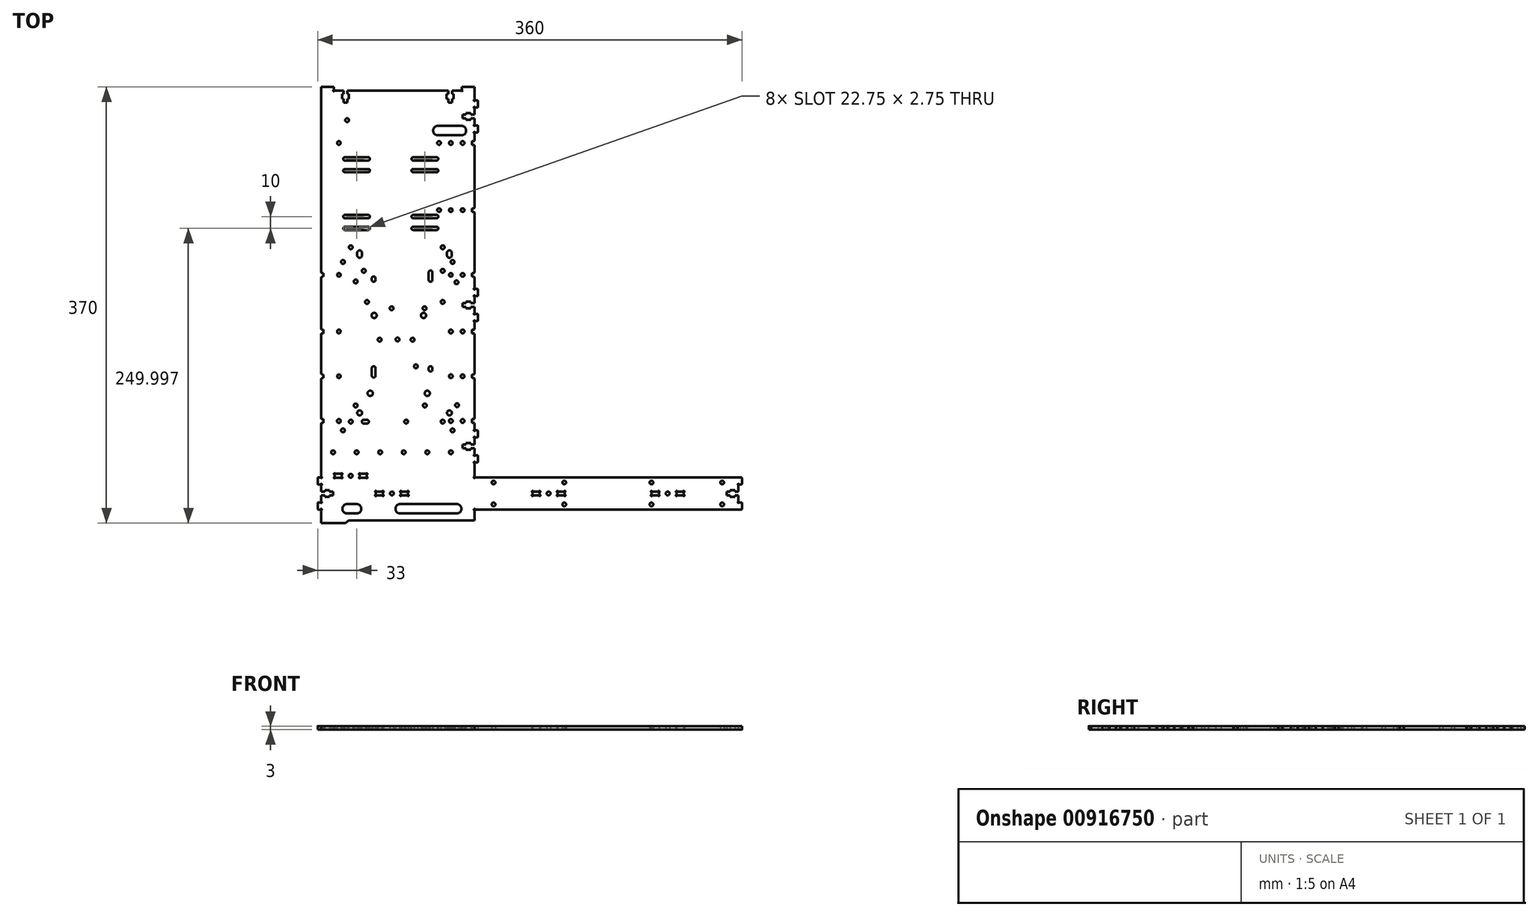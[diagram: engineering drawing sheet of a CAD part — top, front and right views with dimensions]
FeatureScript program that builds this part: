
annotation { "Feature Type Name" : "Feature", "Feature Type Description" : "" }
export const myFeature = defineFeature(function(context is Context, id is Id, definition is map)
    precondition{}
    {
        {
            var Q0;
            Q0=qCreatedBy(makeId("Top.planeOp"),FACE);
            var sketch = newSketch(context, id + "F0", { "sketchPlane" : qUnion([Q0])});
            skCircle(sketch, "E0", {"center": v(103.25, -146.86) * mm, "radius": 1.55 * mm});
            skCircle(sketch, "E1", {"center": v(-30.75, -146.86) * mm, "radius": 1.55 * mm});
            skCircle(sketch, "E2", {"center": v(163.25, -165.45) * mm, "radius": 1.55 * mm});
            skCircle(sketch, "E3", {"center": v(-30.75, -165.45) * mm, "radius": 1.55 * mm});
            skArc(sketch, "E4", {"start": v(104.17, -157.8) * mm, "mid": v(103.92, -157.87) * mm, "end": v(103.73, -158.05) * mm});
            skArc(sketch, "E5", {"start": v(103.05, -157.37) * mm, "mid": v(102.95, -158.16) * mm, "end": v(103.73, -158.05) * mm});
            skArc(sketch, "E6", {"start": v(103.05, -157.37) * mm, "mid": v(103.23, -157.19) * mm, "end": v(103.3, -156.94) * mm});
            skLineSegment(sketch, "E7", {"start": v(103.3, -155.37) * mm, "end": v(103.3, -156.94) * mm});
            skArc(sketch, "E8", {"start": v(103.3, -155.37) * mm, "mid": v(103.23, -155.12) * mm, "end": v(103.05, -154.94) * mm});
            skArc(sketch, "E9", {"start": v(103.73, -154.25) * mm, "mid": v(102.95, -154.15) * mm, "end": v(103.05, -154.94) * mm});
            skArc(sketch, "E10", {"start": v(103.73, -154.25) * mm, "mid": v(103.92, -154.44) * mm, "end": v(104.17, -154.5) * mm});
            skLineSegment(sketch, "E11", {"start": v(108.63, -154.5) * mm, "end": v(104.17, -154.5) * mm});
            skArc(sketch, "E12", {"start": v(108.63, -154.5) * mm, "mid": v(108.88, -154.44) * mm, "end": v(109.07, -154.25) * mm});
            skArc(sketch, "E13", {"start": v(109.75, -154.94) * mm, "mid": v(109.85, -154.15) * mm, "end": v(109.07, -154.25) * mm});
            skArc(sketch, "E14", {"start": v(109.75, -154.94) * mm, "mid": v(109.57, -155.12) * mm, "end": v(109.5, -155.37) * mm});
            skLineSegment(sketch, "E15", {"start": v(109.5, -156.94) * mm, "end": v(109.5, -155.37) * mm});
            skArc(sketch, "E16", {"start": v(109.5, -156.94) * mm, "mid": v(109.57, -157.19) * mm, "end": v(109.75, -157.37) * mm});
            skArc(sketch, "E17", {"start": v(109.07, -158.05) * mm, "mid": v(109.85, -158.16) * mm, "end": v(109.75, -157.37) * mm});
            skArc(sketch, "E18", {"start": v(109.07, -158.05) * mm, "mid": v(108.88, -157.87) * mm, "end": v(108.63, -157.8) * mm});
            skLineSegment(sketch, "E19", {"start": v(104.17, -157.8) * mm, "end": v(108.63, -157.8) * mm});
            skArc(sketch, "E20", {"start": v(125.37, -157.8) * mm, "mid": v(125.12, -157.87) * mm, "end": v(124.93, -158.05) * mm});
            skArc(sketch, "E21", {"start": v(124.25, -157.37) * mm, "mid": v(124.15, -158.16) * mm, "end": v(124.93, -158.05) * mm});
            skArc(sketch, "E22", {"start": v(124.25, -157.37) * mm, "mid": v(124.43, -157.19) * mm, "end": v(124.5, -156.94) * mm});
            skLineSegment(sketch, "E23", {"start": v(124.5, -155.37) * mm, "end": v(124.5, -156.94) * mm});
            skArc(sketch, "E24", {"start": v(124.5, -155.37) * mm, "mid": v(124.43, -155.12) * mm, "end": v(124.25, -154.94) * mm});
            skArc(sketch, "E25", {"start": v(124.93, -154.25) * mm, "mid": v(124.15, -154.15) * mm, "end": v(124.25, -154.94) * mm});
            skArc(sketch, "E26", {"start": v(124.93, -154.25) * mm, "mid": v(125.12, -154.44) * mm, "end": v(125.37, -154.5) * mm});
            skLineSegment(sketch, "E27", {"start": v(129.83, -154.5) * mm, "end": v(125.37, -154.5) * mm});
            skArc(sketch, "E28", {"start": v(129.83, -154.5) * mm, "mid": v(130.08, -154.44) * mm, "end": v(130.27, -154.25) * mm});
            skArc(sketch, "E29", {"start": v(130.95, -154.94) * mm, "mid": v(131.05, -154.15) * mm, "end": v(130.27, -154.25) * mm});
            skArc(sketch, "E30", {"start": v(130.95, -154.94) * mm, "mid": v(130.77, -155.12) * mm, "end": v(130.7, -155.37) * mm});
            skLineSegment(sketch, "E31", {"start": v(130.7, -156.94) * mm, "end": v(130.7, -155.37) * mm});
            skArc(sketch, "E32", {"start": v(130.7, -156.94) * mm, "mid": v(130.77, -157.19) * mm, "end": v(130.95, -157.37) * mm});
            skArc(sketch, "E33", {"start": v(130.27, -158.05) * mm, "mid": v(131.05, -158.16) * mm, "end": v(130.95, -157.37) * mm});
            skArc(sketch, "E34", {"start": v(130.27, -158.05) * mm, "mid": v(130.08, -157.87) * mm, "end": v(129.83, -157.8) * mm});
            skLineSegment(sketch, "E35", {"start": v(125.37, -157.8) * mm, "end": v(129.83, -157.8) * mm});
            skCircle(sketch, "E36", {"center": v(-67, 29.35) * mm, "radius": 1.55 * mm});
            skCircle(sketch, "E37", {"center": v(-77, 84.35) * mm, "radius": 1.55 * mm});
            skCircle(sketch, "E38", {"center": v(-73.88, 52.83) * mm, "radius": 1.6 * mm});
            skCircle(sketch, "E39", {"center": v(-151.88, -95.17) * mm, "radius": 1.6 * mm});
            skCircle(sketch, "E40", {"center": v(-90.17, -5.05) * mm, "radius": 2.23 * mm});
            skCircle(sketch, "E41", {"center": v(-87, -71.15) * mm, "radius": 2.23 * mm});
            skCircle(sketch, "E42", {"center": v(-87, -121.15) * mm, "radius": 1.6 * mm});
            skCircle(sketch, "E43", {"center": v(-127, -121.15) * mm, "radius": 1.6 * mm});
            skCircle(sketch, "E44", {"center": v(-167, -121.15) * mm, "radius": 1.6 * mm});
            skCircle(sketch, "E45", {"center": v(-162, -56.65) * mm, "radius": 1.55 * mm});
            skCircle(sketch, "E46", {"center": v(-162, 29.35) * mm, "radius": 1.55 * mm});
            skCircle(sketch, "E47", {"center": v(-140.88, 32.83) * mm, "radius": 1.6 * mm});
            skCircle(sketch, "E48", {"center": v(-73.88, 32.83) * mm, "radius": 1.6 * mm});
            skCircle(sketch, "E49", {"center": v(-65.5, 40.35) * mm, "radius": 1.6 * mm});
            skCircle(sketch, "E50", {"center": v(-65.5, -102.65) * mm, "radius": 1.6 * mm});
            skCircle(sketch, "E51", {"center": v(-112.23, -25.44) * mm, "radius": 1.6 * mm});
            skCircle(sketch, "E52", {"center": v(-61.73, -81.24) * mm, "radius": 1.6 * mm});
            skCircle(sketch, "E53", {"center": v(-147.73, 23.76) * mm, "radius": 1.6 * mm});
            skCircle(sketch, "E54", {"center": v(-62.23, 23.06) * mm, "radius": 1.6 * mm});
            skCircle(sketch, "E55", {"center": v(-73.88, 6.43) * mm, "radius": 1.6 * mm});
            skLineSegment(sketch, "E56", {"start": v(-134.07, 26.46) * mm, "end": v(-134.07, 25.19) * mm});
            skArc(sketch, "E57", {"start": v(-130.87, 26.46) * mm, "mid": v(-132.47, 28.06) * mm, "end": v(-134.07, 26.46) * mm});
            skLineSegment(sketch, "E58", {"start": v(-130.87, 25.19) * mm, "end": v(-130.87, 26.46) * mm});
            skArc(sketch, "E59", {"start": v(-134.07, 25.19) * mm, "mid": v(-132.47, 23.59) * mm, "end": v(-130.87, 25.19) * mm});
            skCircle(sketch, "E60", {"center": v(-127.39, -25.61) * mm, "radius": 1.6 * mm});
            skCircle(sketch, "E61", {"center": v(-99.45, -25.61) * mm, "radius": 1.6 * mm});
            skCircle(sketch, "E62", {"center": v(-57, 141.35) * mm, "radius": 1.55 * mm});
            skCircle(sketch, "E63", {"center": v(-67, -18.65) * mm, "radius": 1.6 * mm});
            skCircle(sketch, "E64", {"center": v(-67, -94.65) * mm, "radius": 1.6 * mm});
            skCircle(sketch, "E65", {"center": v(-57, -56.65) * mm, "radius": 1.55 * mm});
            skCircle(sketch, "E66", {"center": v(-57, -18.65) * mm, "radius": 1.55 * mm});
            skCircle(sketch, "E67", {"center": v(-152, -141.15) * mm, "radius": 1.6 * mm});
            skArc(sketch, "E68", {"start": v(-129.83, -157.8) * mm, "mid": v(-130.08, -157.87) * mm, "end": v(-130.27, -158.05) * mm});
            skArc(sketch, "E69", {"start": v(-130.95, -157.37) * mm, "mid": v(-131.05, -158.16) * mm, "end": v(-130.27, -158.05) * mm});
            skArc(sketch, "E70", {"start": v(-130.95, -157.37) * mm, "mid": v(-130.77, -157.19) * mm, "end": v(-130.7, -156.94) * mm});
            skLineSegment(sketch, "E71", {"start": v(-130.7, -155.37) * mm, "end": v(-130.7, -156.94) * mm});
            skArc(sketch, "E72", {"start": v(-130.7, -155.37) * mm, "mid": v(-130.77, -155.12) * mm, "end": v(-130.95, -154.94) * mm});
            skArc(sketch, "E73", {"start": v(-130.27, -154.25) * mm, "mid": v(-131.05, -154.15) * mm, "end": v(-130.95, -154.94) * mm});
            skArc(sketch, "E74", {"start": v(-130.27, -154.25) * mm, "mid": v(-130.08, -154.44) * mm, "end": v(-129.83, -154.5) * mm});
            skLineSegment(sketch, "E75", {"start": v(-125.37, -154.5) * mm, "end": v(-129.83, -154.5) * mm});
            skArc(sketch, "E76", {"start": v(-125.37, -154.5) * mm, "mid": v(-125.12, -154.44) * mm, "end": v(-124.93, -154.25) * mm});
            skArc(sketch, "E77", {"start": v(-124.25, -154.94) * mm, "mid": v(-124.15, -154.15) * mm, "end": v(-124.93, -154.25) * mm});
            skArc(sketch, "E78", {"start": v(-124.25, -154.94) * mm, "mid": v(-124.43, -155.12) * mm, "end": v(-124.5, -155.37) * mm});
            skLineSegment(sketch, "E79", {"start": v(-124.5, -156.94) * mm, "end": v(-124.5, -155.37) * mm});
            skArc(sketch, "E80", {"start": v(-124.5, -156.94) * mm, "mid": v(-124.43, -157.19) * mm, "end": v(-124.25, -157.37) * mm});
            skArc(sketch, "E81", {"start": v(-124.93, -158.05) * mm, "mid": v(-124.15, -158.16) * mm, "end": v(-124.25, -157.37) * mm});
            skArc(sketch, "E82", {"start": v(-124.93, -158.05) * mm, "mid": v(-125.12, -157.87) * mm, "end": v(-125.37, -157.8) * mm});
            skLineSegment(sketch, "E83", {"start": v(-129.83, -157.8) * mm, "end": v(-125.37, -157.8) * mm});
            skArc(sketch, "E84", {"start": v(-108.63, -157.8) * mm, "mid": v(-108.88, -157.87) * mm, "end": v(-109.07, -158.05) * mm});
            skArc(sketch, "E85", {"start": v(-109.75, -157.37) * mm, "mid": v(-109.85, -158.16) * mm, "end": v(-109.07, -158.05) * mm});
            skArc(sketch, "E86", {"start": v(-109.75, -157.37) * mm, "mid": v(-109.57, -157.19) * mm, "end": v(-109.5, -156.94) * mm});
            skLineSegment(sketch, "E87", {"start": v(-109.5, -155.37) * mm, "end": v(-109.5, -156.94) * mm});
            skArc(sketch, "E88", {"start": v(-109.5, -155.37) * mm, "mid": v(-109.57, -155.12) * mm, "end": v(-109.75, -154.94) * mm});
            skArc(sketch, "E89", {"start": v(-109.07, -154.25) * mm, "mid": v(-109.85, -154.15) * mm, "end": v(-109.75, -154.94) * mm});
            skArc(sketch, "E90", {"start": v(-109.07, -154.25) * mm, "mid": v(-108.88, -154.44) * mm, "end": v(-108.63, -154.5) * mm});
            skLineSegment(sketch, "E91", {"start": v(-104.17, -154.5) * mm, "end": v(-108.63, -154.5) * mm});
            skArc(sketch, "E92", {"start": v(-104.17, -154.5) * mm, "mid": v(-103.92, -154.44) * mm, "end": v(-103.73, -154.25) * mm});
            skArc(sketch, "E93", {"start": v(-103.05, -154.94) * mm, "mid": v(-102.95, -154.15) * mm, "end": v(-103.73, -154.25) * mm});
            skArc(sketch, "E94", {"start": v(-103.05, -154.94) * mm, "mid": v(-103.23, -155.12) * mm, "end": v(-103.3, -155.37) * mm});
            skLineSegment(sketch, "E95", {"start": v(-103.3, -156.94) * mm, "end": v(-103.3, -155.37) * mm});
            skArc(sketch, "E96", {"start": v(-103.3, -156.94) * mm, "mid": v(-103.23, -157.19) * mm, "end": v(-103.05, -157.37) * mm});
            skArc(sketch, "E97", {"start": v(-103.73, -158.05) * mm, "mid": v(-102.95, -158.16) * mm, "end": v(-103.05, -157.37) * mm});
            skArc(sketch, "E98", {"start": v(-103.73, -158.05) * mm, "mid": v(-103.92, -157.87) * mm, "end": v(-104.17, -157.8) * mm});
            skLineSegment(sketch, "E99", {"start": v(-108.63, -157.8) * mm, "end": v(-104.17, -157.8) * mm});
            skLineSegment(sketch, "E100", {"start": v(-155, -173.15) * mm, "end": v(-147, -173.15) * mm});
            skArc(sketch, "E101", {"start": v(-155, -165.15) * mm, "mid": v(-159, -169.15) * mm, "end": v(-155, -173.15) * mm});
            skLineSegment(sketch, "E102", {"start": v(-147, -165.15) * mm, "end": v(-155, -165.15) * mm});
            skArc(sketch, "E103", {"start": v(-147, -173.15) * mm, "mid": v(-143, -169.15) * mm, "end": v(-147, -165.15) * mm});
            skCircle(sketch, "E104", {"center": v(-155, 160.75) * mm, "radius": 1.6 * mm});
            skCircle(sketch, "E105", {"center": v(16, -156.15) * mm, "radius": 1.6 * mm});
            skArc(sketch, "E106", {"start": v(-47, -170.62) * mm, "mid": v(-47.07, -170.37) * mm, "end": v(-47.25, -170.19) * mm});
            skArc(sketch, "E107", {"start": v(-46.57, -169.5) * mm, "mid": v(-47.35, -169.4) * mm, "end": v(-47.25, -170.19) * mm});
            skArc(sketch, "E108", {"start": v(-46.57, -169.5) * mm, "mid": v(-46.38, -169.69) * mm, "end": v(-46.13, -169.75) * mm});
            skLineSegment(sketch, "E109", {"start": v(-46.13, -169.75) * mm, "end": v(179.5, -169.75) * mm});
            skArc(sketch, "E110", {"start": v(179.5, -169.75) * mm, "mid": v(179.85, -169.6) * mm, "end": v(180, -169.25) * mm});
            skLineSegment(sketch, "E111", {"start": v(180, -169.25) * mm, "end": v(180, -164.25) * mm});
            skArc(sketch, "E112", {"start": v(180, -164.25) * mm, "mid": v(179.85, -163.9) * mm, "end": v(179.5, -163.75) * mm});
            skLineSegment(sketch, "E113", {"start": v(179.5, -163.75) * mm, "end": v(177.87, -163.75) * mm});
            skArc(sketch, "E114", {"start": v(177.87, -163.75) * mm, "mid": v(177.62, -163.82) * mm, "end": v(177.43, -164) * mm});
            skArc(sketch, "E115", {"start": v(176.75, -163.32) * mm, "mid": v(176.65, -164.1) * mm, "end": v(177.43, -164) * mm});
            skArc(sketch, "E116", {"start": v(176.75, -163.32) * mm, "mid": v(176.93, -163.14) * mm, "end": v(177, -162.89) * mm});
            skLineSegment(sketch, "E117", {"start": v(177, -162.89) * mm, "end": v(177, -157.75) * mm});
            skLineSegment(sketch, "E118", {"start": v(177, -157.75) * mm, "end": v(174, -157.75) * mm});
            skLineSegment(sketch, "E119", {"start": v(174, -157.75) * mm, "end": v(174, -159.03) * mm});
            skLineSegment(sketch, "E120", {"start": v(174, -159.03) * mm, "end": v(170, -159.03) * mm});
            skLineSegment(sketch, "E121", {"start": v(170, -159.03) * mm, "end": v(170, -157.75) * mm});
            skLineSegment(sketch, "E122", {"start": v(170, -157.75) * mm, "end": v(167, -157.75) * mm});
            skLineSegment(sketch, "E123", {"start": v(167, -157.75) * mm, "end": v(167, -154.55) * mm});
            skLineSegment(sketch, "E124", {"start": v(167, -154.55) * mm, "end": v(170, -154.55) * mm});
            skLineSegment(sketch, "E125", {"start": v(170, -154.55) * mm, "end": v(170, -153.28) * mm});
            skLineSegment(sketch, "E126", {"start": v(170, -153.28) * mm, "end": v(174, -153.28) * mm});
            skLineSegment(sketch, "E127", {"start": v(174, -153.28) * mm, "end": v(174, -154.55) * mm});
            skLineSegment(sketch, "E128", {"start": v(174, -154.55) * mm, "end": v(177, -154.55) * mm});
            skLineSegment(sketch, "E129", {"start": v(177, -154.55) * mm, "end": v(177, -149.42) * mm});
            skArc(sketch, "E130", {"start": v(177, -149.42) * mm, "mid": v(176.93, -149.17) * mm, "end": v(176.75, -148.99) * mm});
            skArc(sketch, "E131", {"start": v(177.43, -148.3) * mm, "mid": v(176.65, -148.2) * mm, "end": v(176.75, -148.99) * mm});
            skArc(sketch, "E132", {"start": v(177.43, -148.3) * mm, "mid": v(177.62, -148.49) * mm, "end": v(177.87, -148.55) * mm});
            skLineSegment(sketch, "E133", {"start": v(177.87, -148.55) * mm, "end": v(179.5, -148.55) * mm});
            skArc(sketch, "E134", {"start": v(179.5, -148.55) * mm, "mid": v(179.85, -148.4) * mm, "end": v(180, -148.05) * mm});
            skLineSegment(sketch, "E135", {"start": v(180, -148.05) * mm, "end": v(180, -143.05) * mm});
            skArc(sketch, "E136", {"start": v(180, -143.05) * mm, "mid": v(179.85, -142.7) * mm, "end": v(179.5, -142.55) * mm});
            skLineSegment(sketch, "E137", {"start": v(179.5, -142.55) * mm, "end": v(-46.13, -142.55) * mm});
            skArc(sketch, "E138", {"start": v(-46.13, -142.55) * mm, "mid": v(-46.38, -142.62) * mm, "end": v(-46.57, -142.8) * mm});
            skArc(sketch, "E139", {"start": v(-47.25, -142.12) * mm, "mid": v(-47.35, -142.9) * mm, "end": v(-46.57, -142.8) * mm});
            skArc(sketch, "E140", {"start": v(-47.25, -142.12) * mm, "mid": v(-47.07, -141.94) * mm, "end": v(-47, -141.69) * mm});
            skLineSegment(sketch, "E141", {"start": v(-47, -141.69) * mm, "end": v(-47, -130.62) * mm});
            skArc(sketch, "E142", {"start": v(-47, -130.62) * mm, "mid": v(-47.07, -130.37) * mm, "end": v(-47.25, -130.19) * mm});
            skArc(sketch, "E143", {"start": v(-46.57, -129.5) * mm, "mid": v(-47.35, -129.4) * mm, "end": v(-47.25, -130.19) * mm});
            skArc(sketch, "E144", {"start": v(-46.57, -129.5) * mm, "mid": v(-46.38, -129.69) * mm, "end": v(-46.13, -129.75) * mm});
            skLineSegment(sketch, "E145", {"start": v(-46.13, -129.75) * mm, "end": v(-44.5, -129.75) * mm});
            skArc(sketch, "E146", {"start": v(-44.5, -129.75) * mm, "mid": v(-44.15, -129.6) * mm, "end": v(-44, -129.25) * mm});
            skLineSegment(sketch, "E147", {"start": v(-44, -129.25) * mm, "end": v(-44, -124.25) * mm});
            skArc(sketch, "E148", {"start": v(-44, -124.25) * mm, "mid": v(-44.15, -123.9) * mm, "end": v(-44.5, -123.75) * mm});
            skLineSegment(sketch, "E149", {"start": v(-44.5, -123.75) * mm, "end": v(-46.13, -123.75) * mm});
            skArc(sketch, "E150", {"start": v(-46.13, -123.75) * mm, "mid": v(-46.38, -123.82) * mm, "end": v(-46.57, -124) * mm});
            skArc(sketch, "E151", {"start": v(-47.25, -123.32) * mm, "mid": v(-47.35, -124.1) * mm, "end": v(-46.57, -124) * mm});
            skArc(sketch, "E152", {"start": v(-47.25, -123.32) * mm, "mid": v(-47.07, -123.14) * mm, "end": v(-47, -122.89) * mm});
            skLineSegment(sketch, "E153", {"start": v(-47, -122.89) * mm, "end": v(-47, -117.75) * mm});
            skLineSegment(sketch, "E154", {"start": v(-47, -117.75) * mm, "end": v(-50, -117.75) * mm});
            skLineSegment(sketch, "E155", {"start": v(-50, -117.75) * mm, "end": v(-50, -119.03) * mm});
            skLineSegment(sketch, "E156", {"start": v(-50, -119.03) * mm, "end": v(-54, -119.03) * mm});
            skLineSegment(sketch, "E157", {"start": v(-54, -119.03) * mm, "end": v(-54, -117.75) * mm});
            skLineSegment(sketch, "E158", {"start": v(-54, -117.75) * mm, "end": v(-57, -117.75) * mm});
            skLineSegment(sketch, "E159", {"start": v(-57, -117.75) * mm, "end": v(-57, -114.55) * mm});
            skLineSegment(sketch, "E160", {"start": v(-57, -114.55) * mm, "end": v(-54, -114.55) * mm});
            skLineSegment(sketch, "E161", {"start": v(-54, -114.55) * mm, "end": v(-54, -113.28) * mm});
            skLineSegment(sketch, "E162", {"start": v(-54, -113.28) * mm, "end": v(-50, -113.28) * mm});
            skLineSegment(sketch, "E163", {"start": v(-50, -113.28) * mm, "end": v(-50, -114.55) * mm});
            skLineSegment(sketch, "E164", {"start": v(-50, -114.55) * mm, "end": v(-47, -114.55) * mm});
            skLineSegment(sketch, "E165", {"start": v(-47, -114.55) * mm, "end": v(-47, -109.42) * mm});
            skArc(sketch, "E166", {"start": v(-47, -109.42) * mm, "mid": v(-47.07, -109.17) * mm, "end": v(-47.25, -108.99) * mm});
            skArc(sketch, "E167", {"start": v(-46.57, -108.3) * mm, "mid": v(-47.35, -108.2) * mm, "end": v(-47.25, -108.99) * mm});
            skArc(sketch, "E168", {"start": v(-46.57, -108.3) * mm, "mid": v(-46.38, -108.49) * mm, "end": v(-46.13, -108.55) * mm});
            skLineSegment(sketch, "E169", {"start": v(-46.13, -108.55) * mm, "end": v(-44.5, -108.55) * mm});
            skArc(sketch, "E170", {"start": v(-44.5, -108.55) * mm, "mid": v(-44.15, -108.4) * mm, "end": v(-44, -108.05) * mm});
            skLineSegment(sketch, "E171", {"start": v(-44, -108.05) * mm, "end": v(-44, -103.05) * mm});
            skArc(sketch, "E172", {"start": v(-44, -103.05) * mm, "mid": v(-44.15, -102.7) * mm, "end": v(-44.5, -102.55) * mm});
            skLineSegment(sketch, "E173", {"start": v(-44.5, -102.55) * mm, "end": v(-46.13, -102.55) * mm});
            skArc(sketch, "E174", {"start": v(-46.13, -102.55) * mm, "mid": v(-46.38, -102.62) * mm, "end": v(-46.57, -102.8) * mm});
            skArc(sketch, "E175", {"start": v(-47.25, -102.12) * mm, "mid": v(-47.35, -102.9) * mm, "end": v(-46.57, -102.8) * mm});
            skArc(sketch, "E176", {"start": v(-47.25, -102.12) * mm, "mid": v(-47.07, -101.94) * mm, "end": v(-47, -101.69) * mm});
            skLineSegment(sketch, "E177", {"start": v(-47, -101.69) * mm, "end": v(-47, -96.65) * mm});
            skLineSegment(sketch, "E178", {"start": v(-47, -96.65) * mm, "end": v(-47.5, -96.15) * mm});
            skLineSegment(sketch, "E179", {"start": v(-47.5, -96.15) * mm, "end": v(-49, -96.15) * mm});
            skLineSegment(sketch, "E180", {"start": v(-49, -96.15) * mm, "end": v(-49, -93.15) * mm});
            skLineSegment(sketch, "E181", {"start": v(-49, -93.15) * mm, "end": v(-47.5, -93.15) * mm});
            skLineSegment(sketch, "E182", {"start": v(-47.5, -93.15) * mm, "end": v(-47, -92.65) * mm});
            skLineSegment(sketch, "E183", {"start": v(-47, -92.65) * mm, "end": v(-47, -58.65) * mm});
            skLineSegment(sketch, "E184", {"start": v(-47, -58.65) * mm, "end": v(-47.5, -58.15) * mm});
            skLineSegment(sketch, "E185", {"start": v(-47.5, -58.15) * mm, "end": v(-49, -58.15) * mm});
            skLineSegment(sketch, "E186", {"start": v(-49, -58.15) * mm, "end": v(-49, -55.15) * mm});
            skLineSegment(sketch, "E187", {"start": v(-49, -55.15) * mm, "end": v(-47.5, -55.15) * mm});
            skLineSegment(sketch, "E188", {"start": v(-47.5, -55.15) * mm, "end": v(-47, -54.65) * mm});
            skLineSegment(sketch, "E189", {"start": v(-47, -54.65) * mm, "end": v(-47, -20.65) * mm});
            skLineSegment(sketch, "E190", {"start": v(-47, -20.65) * mm, "end": v(-47.5, -20.15) * mm});
            skLineSegment(sketch, "E191", {"start": v(-47.5, -20.15) * mm, "end": v(-49, -20.15) * mm});
            skLineSegment(sketch, "E192", {"start": v(-49, -20.15) * mm, "end": v(-49, -17.15) * mm});
            skLineSegment(sketch, "E193", {"start": v(-49, -17.15) * mm, "end": v(-47.5, -17.15) * mm});
            skLineSegment(sketch, "E194", {"start": v(-47.5, -17.15) * mm, "end": v(-47, -16.65) * mm});
            skLineSegment(sketch, "E195", {"start": v(-47, -16.65) * mm, "end": v(-47, -10.62) * mm});
            skArc(sketch, "E196", {"start": v(-47, -10.62) * mm, "mid": v(-47.07, -10.37) * mm, "end": v(-47.25, -10.19) * mm});
            skArc(sketch, "E197", {"start": v(-46.57, -9.5) * mm, "mid": v(-47.35, -9.4) * mm, "end": v(-47.25, -10.19) * mm});
            skArc(sketch, "E198", {"start": v(-46.57, -9.5) * mm, "mid": v(-46.38, -9.69) * mm, "end": v(-46.13, -9.75) * mm});
            skLineSegment(sketch, "E199", {"start": v(-46.13, -9.75) * mm, "end": v(-44.5, -9.75) * mm});
            skArc(sketch, "E200", {"start": v(-44.5, -9.75) * mm, "mid": v(-44.15, -9.6) * mm, "end": v(-44, -9.25) * mm});
            skLineSegment(sketch, "E201", {"start": v(-44, -9.25) * mm, "end": v(-44, -4.25) * mm});
            skArc(sketch, "E202", {"start": v(-44, -4.25) * mm, "mid": v(-44.15, -3.9) * mm, "end": v(-44.5, -3.75) * mm});
            skLineSegment(sketch, "E203", {"start": v(-44.5, -3.75) * mm, "end": v(-46.13, -3.75) * mm});
            skArc(sketch, "E204", {"start": v(-46.13, -3.75) * mm, "mid": v(-46.38, -3.82) * mm, "end": v(-46.57, -4) * mm});
            skArc(sketch, "E205", {"start": v(-47.25, -3.32) * mm, "mid": v(-47.35, -4.1) * mm, "end": v(-46.57, -4) * mm});
            skArc(sketch, "E206", {"start": v(-47.25, -3.32) * mm, "mid": v(-47.07, -3.14) * mm, "end": v(-47, -2.89) * mm});
            skLineSegment(sketch, "E207", {"start": v(-47, -2.89) * mm, "end": v(-47, 2.25) * mm});
            skLineSegment(sketch, "E208", {"start": v(-47, 2.25) * mm, "end": v(-50, 2.25) * mm});
            skLineSegment(sketch, "E209", {"start": v(-50, 2.25) * mm, "end": v(-50, 0.97) * mm});
            skLineSegment(sketch, "E210", {"start": v(-50, 0.97) * mm, "end": v(-54, 0.97) * mm});
            skLineSegment(sketch, "E211", {"start": v(-54, 0.97) * mm, "end": v(-54, 2.25) * mm});
            skLineSegment(sketch, "E212", {"start": v(-54, 2.25) * mm, "end": v(-57, 2.25) * mm});
            skLineSegment(sketch, "E213", {"start": v(-57, 2.25) * mm, "end": v(-57, 5.45) * mm});
            skLineSegment(sketch, "E214", {"start": v(-57, 5.45) * mm, "end": v(-54, 5.45) * mm});
            skLineSegment(sketch, "E215", {"start": v(-54, 5.45) * mm, "end": v(-54, 6.72) * mm});
            skLineSegment(sketch, "E216", {"start": v(-54, 6.72) * mm, "end": v(-50, 6.72) * mm});
            skLineSegment(sketch, "E217", {"start": v(-50, 6.72) * mm, "end": v(-50, 5.45) * mm});
            skLineSegment(sketch, "E218", {"start": v(-50, 5.45) * mm, "end": v(-47, 5.45) * mm});
            skLineSegment(sketch, "E219", {"start": v(-47, 5.45) * mm, "end": v(-47, 10.58) * mm});
            skArc(sketch, "E220", {"start": v(-47, 10.58) * mm, "mid": v(-47.07, 10.83) * mm, "end": v(-47.25, 11.01) * mm});
            skArc(sketch, "E221", {"start": v(-46.57, 11.7) * mm, "mid": v(-47.35, 11.8) * mm, "end": v(-47.25, 11.01) * mm});
            skArc(sketch, "E222", {"start": v(-46.57, 11.7) * mm, "mid": v(-46.38, 11.51) * mm, "end": v(-46.13, 11.45) * mm});
            skLineSegment(sketch, "E223", {"start": v(-46.13, 11.45) * mm, "end": v(-44.5, 11.45) * mm});
            skArc(sketch, "E224", {"start": v(-44.5, 11.45) * mm, "mid": v(-44.15, 11.6) * mm, "end": v(-44, 11.95) * mm});
            skLineSegment(sketch, "E225", {"start": v(-44, 11.95) * mm, "end": v(-44, 16.95) * mm});
            skArc(sketch, "E226", {"start": v(-44, 16.95) * mm, "mid": v(-44.15, 17.3) * mm, "end": v(-44.5, 17.45) * mm});
            skLineSegment(sketch, "E227", {"start": v(-44.5, 17.45) * mm, "end": v(-46.13, 17.45) * mm});
            skArc(sketch, "E228", {"start": v(-46.13, 17.45) * mm, "mid": v(-46.38, 17.38) * mm, "end": v(-46.57, 17.2) * mm});
            skArc(sketch, "E229", {"start": v(-47.25, 17.88) * mm, "mid": v(-47.35, 17.1) * mm, "end": v(-46.57, 17.2) * mm});
            skArc(sketch, "E230", {"start": v(-47.25, 17.88) * mm, "mid": v(-47.07, 18.06) * mm, "end": v(-47, 18.31) * mm});
            skLineSegment(sketch, "E231", {"start": v(-47, 18.31) * mm, "end": v(-47, 27.35) * mm});
            skLineSegment(sketch, "E232", {"start": v(-47, 27.35) * mm, "end": v(-47.5, 27.85) * mm});
            skLineSegment(sketch, "E233", {"start": v(-47.5, 27.85) * mm, "end": v(-49, 27.85) * mm});
            skLineSegment(sketch, "E234", {"start": v(-49, 27.85) * mm, "end": v(-49, 30.85) * mm});
            skLineSegment(sketch, "E235", {"start": v(-49, 30.85) * mm, "end": v(-47.5, 30.85) * mm});
            skLineSegment(sketch, "E236", {"start": v(-47.5, 30.85) * mm, "end": v(-47, 31.35) * mm});
            skLineSegment(sketch, "E237", {"start": v(-47, 31.35) * mm, "end": v(-47, 82.35) * mm});
            skLineSegment(sketch, "E238", {"start": v(-47, 82.35) * mm, "end": v(-47.5, 82.85) * mm});
            skLineSegment(sketch, "E239", {"start": v(-47.5, 82.85) * mm, "end": v(-49, 82.85) * mm});
            skLineSegment(sketch, "E240", {"start": v(-49, 82.85) * mm, "end": v(-49, 85.85) * mm});
            skLineSegment(sketch, "E241", {"start": v(-49, 85.85) * mm, "end": v(-47.5, 85.85) * mm});
            skLineSegment(sketch, "E242", {"start": v(-47.5, 85.85) * mm, "end": v(-47, 86.35) * mm});
            skLineSegment(sketch, "E243", {"start": v(-47, 86.35) * mm, "end": v(-47, 139.35) * mm});
            skLineSegment(sketch, "E244", {"start": v(-47, 139.35) * mm, "end": v(-47.5, 139.85) * mm});
            skLineSegment(sketch, "E245", {"start": v(-47.5, 139.85) * mm, "end": v(-49, 139.85) * mm});
            skLineSegment(sketch, "E246", {"start": v(-49, 139.85) * mm, "end": v(-49, 142.85) * mm});
            skLineSegment(sketch, "E247", {"start": v(-49, 142.85) * mm, "end": v(-47.5, 142.85) * mm});
            skLineSegment(sketch, "E248", {"start": v(-47.5, 142.85) * mm, "end": v(-47, 143.35) * mm});
            skLineSegment(sketch, "E249", {"start": v(-47, 143.35) * mm, "end": v(-47, 149.38) * mm});
            skArc(sketch, "E250", {"start": v(-47, 149.38) * mm, "mid": v(-47.07, 149.63) * mm, "end": v(-47.25, 149.81) * mm});
            skArc(sketch, "E251", {"start": v(-46.57, 150.5) * mm, "mid": v(-47.35, 150.6) * mm, "end": v(-47.25, 149.81) * mm});
            skArc(sketch, "E252", {"start": v(-46.57, 150.5) * mm, "mid": v(-46.38, 150.31) * mm, "end": v(-46.13, 150.25) * mm});
            skLineSegment(sketch, "E253", {"start": v(-46.13, 150.25) * mm, "end": v(-44.5, 150.25) * mm});
            skArc(sketch, "E254", {"start": v(-44.5, 150.25) * mm, "mid": v(-44.15, 150.4) * mm, "end": v(-44, 150.75) * mm});
            skLineSegment(sketch, "E255", {"start": v(-44, 150.75) * mm, "end": v(-44, 155.75) * mm});
            skArc(sketch, "E256", {"start": v(-44, 155.75) * mm, "mid": v(-44.15, 156.1) * mm, "end": v(-44.5, 156.25) * mm});
            skLineSegment(sketch, "E257", {"start": v(-44.5, 156.25) * mm, "end": v(-46.13, 156.25) * mm});
            skArc(sketch, "E258", {"start": v(-46.13, 156.25) * mm, "mid": v(-46.38, 156.18) * mm, "end": v(-46.57, 156) * mm});
            skArc(sketch, "E259", {"start": v(-47.25, 156.68) * mm, "mid": v(-47.35, 155.9) * mm, "end": v(-46.57, 156) * mm});
            skArc(sketch, "E260", {"start": v(-47.25, 156.68) * mm, "mid": v(-47.07, 156.86) * mm, "end": v(-47, 157.11) * mm});
            skLineSegment(sketch, "E261", {"start": v(-47, 157.11) * mm, "end": v(-47, 162.25) * mm});
            skLineSegment(sketch, "E262", {"start": v(-47, 162.25) * mm, "end": v(-50, 162.25) * mm});
            skLineSegment(sketch, "E263", {"start": v(-50, 162.25) * mm, "end": v(-50, 160.97) * mm});
            skLineSegment(sketch, "E264", {"start": v(-50, 160.97) * mm, "end": v(-54, 160.97) * mm});
            skLineSegment(sketch, "E265", {"start": v(-54, 160.97) * mm, "end": v(-54, 162.25) * mm});
            skLineSegment(sketch, "E266", {"start": v(-54, 162.25) * mm, "end": v(-57, 162.25) * mm});
            skLineSegment(sketch, "E267", {"start": v(-57, 162.25) * mm, "end": v(-57, 165.45) * mm});
            skLineSegment(sketch, "E268", {"start": v(-57, 165.45) * mm, "end": v(-54, 165.45) * mm});
            skLineSegment(sketch, "E269", {"start": v(-54, 165.45) * mm, "end": v(-54, 166.72) * mm});
            skLineSegment(sketch, "E270", {"start": v(-54, 166.72) * mm, "end": v(-50, 166.72) * mm});
            skLineSegment(sketch, "E271", {"start": v(-50, 166.72) * mm, "end": v(-50, 165.45) * mm});
            skLineSegment(sketch, "E272", {"start": v(-50, 165.45) * mm, "end": v(-47, 165.45) * mm});
            skLineSegment(sketch, "E273", {"start": v(-47, 165.45) * mm, "end": v(-47, 170.58) * mm});
            skArc(sketch, "E274", {"start": v(-47, 170.58) * mm, "mid": v(-47.07, 170.83) * mm, "end": v(-47.25, 171.01) * mm});
            skArc(sketch, "E275", {"start": v(-46.57, 171.7) * mm, "mid": v(-47.35, 171.8) * mm, "end": v(-47.25, 171.01) * mm});
            skArc(sketch, "E276", {"start": v(-46.57, 171.7) * mm, "mid": v(-46.38, 171.51) * mm, "end": v(-46.13, 171.45) * mm});
            skLineSegment(sketch, "E277", {"start": v(-46.13, 171.45) * mm, "end": v(-44.5, 171.45) * mm});
            skArc(sketch, "E278", {"start": v(-44.5, 171.45) * mm, "mid": v(-44.15, 171.6) * mm, "end": v(-44, 171.95) * mm});
            skLineSegment(sketch, "E279", {"start": v(-44, 171.95) * mm, "end": v(-44, 176.95) * mm});
            skArc(sketch, "E280", {"start": v(-44, 176.95) * mm, "mid": v(-44.15, 177.3) * mm, "end": v(-44.5, 177.45) * mm});
            skLineSegment(sketch, "E281", {"start": v(-44.5, 177.45) * mm, "end": v(-46.13, 177.45) * mm});
            skArc(sketch, "E282", {"start": v(-46.13, 177.45) * mm, "mid": v(-46.38, 177.38) * mm, "end": v(-46.57, 177.2) * mm});
            skArc(sketch, "E283", {"start": v(-47.25, 177.88) * mm, "mid": v(-47.35, 177.1) * mm, "end": v(-46.57, 177.2) * mm});
            skArc(sketch, "E284", {"start": v(-47.25, 177.88) * mm, "mid": v(-47.07, 178.06) * mm, "end": v(-47, 178.31) * mm});
            skLineSegment(sketch, "E285", {"start": v(-47, 178.31) * mm, "end": v(-47, 188.85) * mm});
            skLineSegment(sketch, "E286", {"start": v(-47, 188.85) * mm, "end": v(-57.65, 188.85) * mm});
            skLineSegment(sketch, "E287", {"start": v(-57.65, 188.85) * mm, "end": v(-57.65, 186.61) * mm});
            skArc(sketch, "E288", {"start": v(-57.65, 186.61) * mm, "mid": v(-57.58, 186.36) * mm, "end": v(-57.4, 186.18) * mm});
            skArc(sketch, "E289", {"start": v(-58.08, 185.5) * mm, "mid": v(-57.3, 185.4) * mm, "end": v(-57.4, 186.18) * mm});
            skArc(sketch, "E290", {"start": v(-58.08, 185.5) * mm, "mid": v(-58.27, 185.68) * mm, "end": v(-58.52, 185.75) * mm});
            skLineSegment(sketch, "E291", {"start": v(-58.52, 185.75) * mm, "end": v(-66.05, 185.75) * mm});
            skLineSegment(sketch, "E292", {"start": v(-66.05, 185.75) * mm, "end": v(-66.05, 182.75) * mm});
            skLineSegment(sketch, "E293", {"start": v(-66.05, 182.75) * mm, "end": v(-64.78, 182.75) * mm});
            skLineSegment(sketch, "E294", {"start": v(-64.78, 182.75) * mm, "end": v(-64.78, 178.75) * mm});
            skLineSegment(sketch, "E295", {"start": v(-64.78, 178.75) * mm, "end": v(-66.05, 178.75) * mm});
            skLineSegment(sketch, "E296", {"start": v(-66.05, 178.75) * mm, "end": v(-66.05, 175.75) * mm});
            skLineSegment(sketch, "E297", {"start": v(-66.05, 175.75) * mm, "end": v(-69.25, 175.75) * mm});
            skLineSegment(sketch, "E298", {"start": v(-69.25, 175.75) * mm, "end": v(-69.25, 178.75) * mm});
            skLineSegment(sketch, "E299", {"start": v(-69.25, 178.75) * mm, "end": v(-70.53, 178.75) * mm});
            skLineSegment(sketch, "E300", {"start": v(-70.53, 178.75) * mm, "end": v(-70.53, 182.75) * mm});
            skLineSegment(sketch, "E301", {"start": v(-70.53, 182.75) * mm, "end": v(-69.25, 182.75) * mm});
            skLineSegment(sketch, "E302", {"start": v(-69.25, 182.75) * mm, "end": v(-69.25, 185.75) * mm});
            skLineSegment(sketch, "E303", {"start": v(-69.25, 185.75) * mm, "end": v(-154.75, 185.75) * mm});
            skLineSegment(sketch, "E304", {"start": v(-154.75, 185.75) * mm, "end": v(-154.75, 182.75) * mm});
            skLineSegment(sketch, "E305", {"start": v(-154.75, 182.75) * mm, "end": v(-153.47, 182.75) * mm});
            skLineSegment(sketch, "E306", {"start": v(-153.47, 182.75) * mm, "end": v(-153.47, 178.75) * mm});
            skLineSegment(sketch, "E307", {"start": v(-153.47, 178.75) * mm, "end": v(-154.75, 178.75) * mm});
            skLineSegment(sketch, "E308", {"start": v(-154.75, 178.75) * mm, "end": v(-154.75, 175.75) * mm});
            skLineSegment(sketch, "E309", {"start": v(-154.75, 175.75) * mm, "end": v(-157.95, 175.75) * mm});
            skLineSegment(sketch, "E310", {"start": v(-157.95, 175.75) * mm, "end": v(-157.95, 178.75) * mm});
            skLineSegment(sketch, "E311", {"start": v(-157.95, 178.75) * mm, "end": v(-159.22, 178.75) * mm});
            skLineSegment(sketch, "E312", {"start": v(-159.22, 178.75) * mm, "end": v(-159.22, 182.75) * mm});
            skLineSegment(sketch, "E313", {"start": v(-159.22, 182.75) * mm, "end": v(-157.95, 182.75) * mm});
            skLineSegment(sketch, "E314", {"start": v(-157.95, 182.75) * mm, "end": v(-157.95, 185.75) * mm});
            skLineSegment(sketch, "E315", {"start": v(-157.95, 185.75) * mm, "end": v(-165.48, 185.75) * mm});
            skArc(sketch, "E316", {"start": v(-165.48, 185.75) * mm, "mid": v(-165.73, 185.68) * mm, "end": v(-165.92, 185.5) * mm});
            skArc(sketch, "E317", {"start": v(-166.6, 186.18) * mm, "mid": v(-166.7, 185.4) * mm, "end": v(-165.92, 185.5) * mm});
            skArc(sketch, "E318", {"start": v(-166.6, 186.18) * mm, "mid": v(-166.42, 186.36) * mm, "end": v(-166.35, 186.61) * mm});
            skLineSegment(sketch, "E319", {"start": v(-166.35, 186.61) * mm, "end": v(-166.35, 188.85) * mm});
            skLineSegment(sketch, "E320", {"start": v(-166.35, 188.85) * mm, "end": v(-177, 188.85) * mm});
            skLineSegment(sketch, "E321", {"start": v(-177, 188.85) * mm, "end": v(-177, 31.85) * mm});
            skArc(sketch, "E322", {"start": v(-177, 31.85) * mm, "mid": v(-176.7, 31.14) * mm, "end": v(-176, 30.85) * mm});
            skLineSegment(sketch, "E323", {"start": v(-176, 30.85) * mm, "end": v(-175, 30.85) * mm});
            skLineSegment(sketch, "E324", {"start": v(-175, 30.85) * mm, "end": v(-175, 27.85) * mm});
            skLineSegment(sketch, "E325", {"start": v(-175, 27.85) * mm, "end": v(-176, 27.85) * mm});
            skArc(sketch, "E326", {"start": v(-176, 27.85) * mm, "mid": v(-176.7, 27.55) * mm, "end": v(-177, 26.85) * mm});
            skLineSegment(sketch, "E327", {"start": v(-177, 26.85) * mm, "end": v(-177, -16.15) * mm});
            skArc(sketch, "E328", {"start": v(-177, -16.15) * mm, "mid": v(-176.7, -16.86) * mm, "end": v(-176, -17.15) * mm});
            skLineSegment(sketch, "E329", {"start": v(-176, -17.15) * mm, "end": v(-175, -17.15) * mm});
            skLineSegment(sketch, "E330", {"start": v(-175, -17.15) * mm, "end": v(-175, -20.15) * mm});
            skLineSegment(sketch, "E331", {"start": v(-175, -20.15) * mm, "end": v(-176, -20.15) * mm});
            skArc(sketch, "E332", {"start": v(-176, -20.15) * mm, "mid": v(-176.7, -20.45) * mm, "end": v(-177, -21.15) * mm});
            skLineSegment(sketch, "E333", {"start": v(-177, -21.15) * mm, "end": v(-177, -54.15) * mm});
            skArc(sketch, "E334", {"start": v(-177, -54.15) * mm, "mid": v(-176.7, -54.86) * mm, "end": v(-176, -55.15) * mm});
            skLineSegment(sketch, "E335", {"start": v(-176, -55.15) * mm, "end": v(-175, -55.15) * mm});
            skLineSegment(sketch, "E336", {"start": v(-175, -55.15) * mm, "end": v(-175, -58.15) * mm});
            skLineSegment(sketch, "E337", {"start": v(-175, -58.15) * mm, "end": v(-176, -58.15) * mm});
            skArc(sketch, "E338", {"start": v(-176, -58.15) * mm, "mid": v(-176.7, -58.45) * mm, "end": v(-177, -59.15) * mm});
            skLineSegment(sketch, "E339", {"start": v(-177, -59.15) * mm, "end": v(-177, -92.15) * mm});
            skArc(sketch, "E340", {"start": v(-177, -92.15) * mm, "mid": v(-176.7, -92.86) * mm, "end": v(-176, -93.15) * mm});
            skLineSegment(sketch, "E341", {"start": v(-176, -93.15) * mm, "end": v(-175, -93.15) * mm});
            skLineSegment(sketch, "E342", {"start": v(-175, -93.15) * mm, "end": v(-175, -96.15) * mm});
            skLineSegment(sketch, "E343", {"start": v(-175, -96.15) * mm, "end": v(-176, -96.15) * mm});
            skArc(sketch, "E344", {"start": v(-176, -96.15) * mm, "mid": v(-176.7, -96.45) * mm, "end": v(-177, -97.15) * mm});
            skLineSegment(sketch, "E345", {"start": v(-177, -97.15) * mm, "end": v(-177, -141.69) * mm});
            skArc(sketch, "E346", {"start": v(-177, -141.69) * mm, "mid": v(-176.93, -141.94) * mm, "end": v(-176.75, -142.12) * mm});
            skArc(sketch, "E347", {"start": v(-177.43, -142.8) * mm, "mid": v(-176.65, -142.9) * mm, "end": v(-176.75, -142.12) * mm});
            skArc(sketch, "E348", {"start": v(-177.43, -142.8) * mm, "mid": v(-177.62, -142.62) * mm, "end": v(-177.87, -142.55) * mm});
            skLineSegment(sketch, "E349", {"start": v(-177.87, -142.55) * mm, "end": v(-179.5, -142.55) * mm});
            skArc(sketch, "E350", {"start": v(-179.5, -142.55) * mm, "mid": v(-179.85, -142.7) * mm, "end": v(-180, -143.05) * mm});
            skLineSegment(sketch, "E351", {"start": v(-180, -143.05) * mm, "end": v(-180, -148.05) * mm});
            skArc(sketch, "E352", {"start": v(-180, -148.05) * mm, "mid": v(-179.85, -148.4) * mm, "end": v(-179.5, -148.55) * mm});
            skLineSegment(sketch, "E353", {"start": v(-179.5, -148.55) * mm, "end": v(-177.87, -148.55) * mm});
            skArc(sketch, "E354", {"start": v(-177.87, -148.55) * mm, "mid": v(-177.62, -148.49) * mm, "end": v(-177.43, -148.3) * mm});
            skArc(sketch, "E355", {"start": v(-176.75, -148.99) * mm, "mid": v(-176.65, -148.2) * mm, "end": v(-177.43, -148.3) * mm});
            skArc(sketch, "E356", {"start": v(-176.75, -148.99) * mm, "mid": v(-176.93, -149.17) * mm, "end": v(-177, -149.42) * mm});
            skLineSegment(sketch, "E357", {"start": v(-177, -149.42) * mm, "end": v(-177, -154.55) * mm});
            skLineSegment(sketch, "E358", {"start": v(-177, -154.55) * mm, "end": v(-174, -154.55) * mm});
            skLineSegment(sketch, "E359", {"start": v(-174, -154.55) * mm, "end": v(-174, -153.28) * mm});
            skLineSegment(sketch, "E360", {"start": v(-174, -153.28) * mm, "end": v(-170, -153.28) * mm});
            skLineSegment(sketch, "E361", {"start": v(-170, -153.28) * mm, "end": v(-170, -154.55) * mm});
            skLineSegment(sketch, "E362", {"start": v(-170, -154.55) * mm, "end": v(-167, -154.55) * mm});
            skLineSegment(sketch, "E363", {"start": v(-167, -154.55) * mm, "end": v(-167, -157.75) * mm});
            skLineSegment(sketch, "E364", {"start": v(-167, -157.75) * mm, "end": v(-170, -157.75) * mm});
            skLineSegment(sketch, "E365", {"start": v(-170, -157.75) * mm, "end": v(-170, -159.03) * mm});
            skLineSegment(sketch, "E366", {"start": v(-170, -159.03) * mm, "end": v(-174, -159.03) * mm});
            skLineSegment(sketch, "E367", {"start": v(-174, -159.03) * mm, "end": v(-174, -157.75) * mm});
            skLineSegment(sketch, "E368", {"start": v(-174, -157.75) * mm, "end": v(-177, -157.75) * mm});
            skLineSegment(sketch, "E369", {"start": v(-177, -157.75) * mm, "end": v(-177, -162.89) * mm});
            skArc(sketch, "E370", {"start": v(-177, -162.89) * mm, "mid": v(-176.93, -163.14) * mm, "end": v(-176.75, -163.32) * mm});
            skArc(sketch, "E371", {"start": v(-177.43, -164) * mm, "mid": v(-176.65, -164.1) * mm, "end": v(-176.75, -163.32) * mm});
            skArc(sketch, "E372", {"start": v(-177.43, -164) * mm, "mid": v(-177.62, -163.82) * mm, "end": v(-177.87, -163.75) * mm});
            skLineSegment(sketch, "E373", {"start": v(-177.87, -163.75) * mm, "end": v(-179.5, -163.75) * mm});
            skArc(sketch, "E374", {"start": v(-179.5, -163.75) * mm, "mid": v(-179.85, -163.9) * mm, "end": v(-180, -164.25) * mm});
            skLineSegment(sketch, "E375", {"start": v(-180, -164.25) * mm, "end": v(-180, -169.25) * mm});
            skArc(sketch, "E376", {"start": v(-180, -169.25) * mm, "mid": v(-179.85, -169.6) * mm, "end": v(-179.5, -169.75) * mm});
            skLineSegment(sketch, "E377", {"start": v(-179.5, -169.75) * mm, "end": v(-177.87, -169.75) * mm});
            skArc(sketch, "E378", {"start": v(-177.87, -169.75) * mm, "mid": v(-177.62, -169.69) * mm, "end": v(-177.43, -169.5) * mm});
            skArc(sketch, "E379", {"start": v(-176.75, -170.19) * mm, "mid": v(-176.65, -169.4) * mm, "end": v(-177.43, -169.5) * mm});
            skArc(sketch, "E380", {"start": v(-176.75, -170.19) * mm, "mid": v(-176.93, -170.37) * mm, "end": v(-177, -170.62) * mm});
            skLineSegment(sketch, "E381", {"start": v(-177, -170.62) * mm, "end": v(-177, -181.15) * mm});
            skLineSegment(sketch, "E382", {"start": v(-177, -181.15) * mm, "end": v(-156.83, -181.15) * mm});
            skArc(sketch, "E383", {"start": v(-156.83, -181.15) * mm, "mid": v(-156.06, -181) * mm, "end": v(-155.41, -180.57) * mm});
            skLineSegment(sketch, "E384", {"start": v(-155.41, -180.57) * mm, "end": v(-154.59, -179.74) * mm});
            skArc(sketch, "E385", {"start": v(-153.17, -179.15) * mm, "mid": v(-153.94, -179.3) * mm, "end": v(-154.59, -179.74) * mm});
            skLineSegment(sketch, "E386", {"start": v(-153.17, -179.15) * mm, "end": v(-47, -179.15) * mm});
            skLineSegment(sketch, "E387", {"start": v(-47, -179.15) * mm, "end": v(-47, -170.62) * mm});
            skLineSegment(sketch, "E388", {"start": v(-62, -165.15) * mm, "end": v(-110, -165.15) * mm});
            skArc(sketch, "E389", {"start": v(-62, -173.15) * mm, "mid": v(-58, -169.15) * mm, "end": v(-62, -165.15) * mm});
            skLineSegment(sketch, "E390", {"start": v(-110, -173.15) * mm, "end": v(-62, -173.15) * mm});
            skArc(sketch, "E391", {"start": v(-110, -165.15) * mm, "mid": v(-114, -169.15) * mm, "end": v(-110, -173.15) * mm});
            skArc(sketch, "E392", {"start": v(24.37, -157.8) * mm, "mid": v(24.12, -157.87) * mm, "end": v(23.93, -158.05) * mm});
            skArc(sketch, "E393", {"start": v(23.25, -157.37) * mm, "mid": v(23.15, -158.16) * mm, "end": v(23.93, -158.05) * mm});
            skArc(sketch, "E394", {"start": v(23.25, -157.37) * mm, "mid": v(23.43, -157.19) * mm, "end": v(23.5, -156.94) * mm});
            skLineSegment(sketch, "E395", {"start": v(23.5, -155.37) * mm, "end": v(23.5, -156.94) * mm});
            skArc(sketch, "E396", {"start": v(23.5, -155.37) * mm, "mid": v(23.43, -155.12) * mm, "end": v(23.25, -154.94) * mm});
            skArc(sketch, "E397", {"start": v(23.93, -154.25) * mm, "mid": v(23.15, -154.15) * mm, "end": v(23.25, -154.94) * mm});
            skArc(sketch, "E398", {"start": v(23.93, -154.25) * mm, "mid": v(24.12, -154.44) * mm, "end": v(24.37, -154.5) * mm});
            skLineSegment(sketch, "E399", {"start": v(28.83, -154.5) * mm, "end": v(24.37, -154.5) * mm});
            skArc(sketch, "E400", {"start": v(28.83, -154.5) * mm, "mid": v(29.08, -154.44) * mm, "end": v(29.27, -154.25) * mm});
            skArc(sketch, "E401", {"start": v(29.95, -154.94) * mm, "mid": v(30.05, -154.15) * mm, "end": v(29.27, -154.25) * mm});
            skArc(sketch, "E402", {"start": v(29.95, -154.94) * mm, "mid": v(29.77, -155.12) * mm, "end": v(29.7, -155.37) * mm});
            skLineSegment(sketch, "E403", {"start": v(29.7, -156.94) * mm, "end": v(29.7, -155.37) * mm});
            skArc(sketch, "E404", {"start": v(29.7, -156.94) * mm, "mid": v(29.77, -157.19) * mm, "end": v(29.95, -157.37) * mm});
            skArc(sketch, "E405", {"start": v(29.27, -158.05) * mm, "mid": v(30.05, -158.16) * mm, "end": v(29.95, -157.37) * mm});
            skArc(sketch, "E406", {"start": v(29.27, -158.05) * mm, "mid": v(29.08, -157.87) * mm, "end": v(28.83, -157.8) * mm});
            skLineSegment(sketch, "E407", {"start": v(24.37, -157.8) * mm, "end": v(28.83, -157.8) * mm});
            skArc(sketch, "E408", {"start": v(3.17, -157.8) * mm, "mid": v(2.92, -157.87) * mm, "end": v(2.73, -158.05) * mm});
            skArc(sketch, "E409", {"start": v(2.05, -157.37) * mm, "mid": v(1.95, -158.16) * mm, "end": v(2.73, -158.05) * mm});
            skArc(sketch, "E410", {"start": v(2.05, -157.37) * mm, "mid": v(2.23, -157.19) * mm, "end": v(2.3, -156.94) * mm});
            skLineSegment(sketch, "E411", {"start": v(2.3, -155.37) * mm, "end": v(2.3, -156.94) * mm});
            skArc(sketch, "E412", {"start": v(2.3, -155.37) * mm, "mid": v(2.23, -155.12) * mm, "end": v(2.05, -154.94) * mm});
            skArc(sketch, "E413", {"start": v(2.73, -154.25) * mm, "mid": v(1.95, -154.15) * mm, "end": v(2.05, -154.94) * mm});
            skArc(sketch, "E414", {"start": v(2.73, -154.25) * mm, "mid": v(2.92, -154.44) * mm, "end": v(3.17, -154.5) * mm});
            skLineSegment(sketch, "E415", {"start": v(7.63, -154.5) * mm, "end": v(3.17, -154.5) * mm});
            skArc(sketch, "E416", {"start": v(7.63, -154.5) * mm, "mid": v(7.88, -154.44) * mm, "end": v(8.07, -154.25) * mm});
            skArc(sketch, "E417", {"start": v(8.75, -154.94) * mm, "mid": v(8.85, -154.15) * mm, "end": v(8.07, -154.25) * mm});
            skArc(sketch, "E418", {"start": v(8.75, -154.94) * mm, "mid": v(8.57, -155.12) * mm, "end": v(8.5, -155.37) * mm});
            skLineSegment(sketch, "E419", {"start": v(8.5, -156.94) * mm, "end": v(8.5, -155.37) * mm});
            skArc(sketch, "E420", {"start": v(8.5, -156.94) * mm, "mid": v(8.57, -157.19) * mm, "end": v(8.75, -157.37) * mm});
            skArc(sketch, "E421", {"start": v(8.07, -158.05) * mm, "mid": v(8.85, -158.16) * mm, "end": v(8.75, -157.37) * mm});
            skArc(sketch, "E422", {"start": v(8.07, -158.05) * mm, "mid": v(7.88, -157.87) * mm, "end": v(7.63, -157.8) * mm});
            skLineSegment(sketch, "E423", {"start": v(3.17, -157.8) * mm, "end": v(7.63, -157.8) * mm});
            skCircle(sketch, "E424", {"center": v(-162, 141.35) * mm, "radius": 1.55 * mm});
            skLineSegment(sketch, "E425", {"start": v(-78, 147.85) * mm, "end": v(-58, 147.85) * mm});
            skArc(sketch, "E426", {"start": v(-78, 155.85) * mm, "mid": v(-82, 151.85) * mm, "end": v(-78, 147.85) * mm});
            skLineSegment(sketch, "E427", {"start": v(-58, 155.85) * mm, "end": v(-78, 155.85) * mm});
            skArc(sketch, "E428", {"start": v(-58, 147.85) * mm, "mid": v(-54, 151.85) * mm, "end": v(-58, 155.85) * mm});
            skCircle(sketch, "E429", {"center": v(-117, -156.15) * mm, "radius": 1.6 * mm});
            skArc(sketch, "E430", {"start": v(-143.63, -142.8) * mm, "mid": v(-143.88, -142.87) * mm, "end": v(-144.07, -143.05) * mm});
            skArc(sketch, "E431", {"start": v(-144.75, -142.37) * mm, "mid": v(-144.85, -143.16) * mm, "end": v(-144.07, -143.05) * mm});
            skArc(sketch, "E432", {"start": v(-144.75, -142.37) * mm, "mid": v(-144.57, -142.19) * mm, "end": v(-144.5, -141.94) * mm});
            skLineSegment(sketch, "E433", {"start": v(-144.5, -140.37) * mm, "end": v(-144.5, -141.94) * mm});
            skArc(sketch, "E434", {"start": v(-144.5, -140.37) * mm, "mid": v(-144.57, -140.12) * mm, "end": v(-144.75, -139.94) * mm});
            skArc(sketch, "E435", {"start": v(-144.07, -139.25) * mm, "mid": v(-144.85, -139.15) * mm, "end": v(-144.75, -139.94) * mm});
            skArc(sketch, "E436", {"start": v(-144.07, -139.25) * mm, "mid": v(-143.88, -139.44) * mm, "end": v(-143.63, -139.5) * mm});
            skLineSegment(sketch, "E437", {"start": v(-139.17, -139.5) * mm, "end": v(-143.63, -139.5) * mm});
            skArc(sketch, "E438", {"start": v(-139.17, -139.5) * mm, "mid": v(-138.92, -139.44) * mm, "end": v(-138.73, -139.25) * mm});
            skArc(sketch, "E439", {"start": v(-138.05, -139.94) * mm, "mid": v(-137.95, -139.15) * mm, "end": v(-138.73, -139.25) * mm});
            skArc(sketch, "E440", {"start": v(-138.05, -139.94) * mm, "mid": v(-138.23, -140.12) * mm, "end": v(-138.3, -140.37) * mm});
            skLineSegment(sketch, "E441", {"start": v(-138.3, -141.94) * mm, "end": v(-138.3, -140.37) * mm});
            skArc(sketch, "E442", {"start": v(-138.3, -141.94) * mm, "mid": v(-138.23, -142.19) * mm, "end": v(-138.05, -142.37) * mm});
            skArc(sketch, "E443", {"start": v(-138.73, -143.05) * mm, "mid": v(-137.95, -143.16) * mm, "end": v(-138.05, -142.37) * mm});
            skArc(sketch, "E444", {"start": v(-138.73, -143.05) * mm, "mid": v(-138.92, -142.87) * mm, "end": v(-139.17, -142.8) * mm});
            skLineSegment(sketch, "E445", {"start": v(-143.63, -142.8) * mm, "end": v(-139.17, -142.8) * mm});
            skArc(sketch, "E446", {"start": v(-164.83, -142.8) * mm, "mid": v(-165.08, -142.87) * mm, "end": v(-165.27, -143.05) * mm});
            skArc(sketch, "E447", {"start": v(-165.95, -142.37) * mm, "mid": v(-166.05, -143.16) * mm, "end": v(-165.27, -143.05) * mm});
            skArc(sketch, "E448", {"start": v(-165.95, -142.37) * mm, "mid": v(-165.77, -142.19) * mm, "end": v(-165.7, -141.94) * mm});
            skLineSegment(sketch, "E449", {"start": v(-165.7, -140.37) * mm, "end": v(-165.7, -141.94) * mm});
            skArc(sketch, "E450", {"start": v(-165.7, -140.37) * mm, "mid": v(-165.77, -140.12) * mm, "end": v(-165.95, -139.94) * mm});
            skArc(sketch, "E451", {"start": v(-165.27, -139.25) * mm, "mid": v(-166.05, -139.15) * mm, "end": v(-165.95, -139.94) * mm});
            skArc(sketch, "E452", {"start": v(-165.27, -139.25) * mm, "mid": v(-165.08, -139.44) * mm, "end": v(-164.83, -139.5) * mm});
            skLineSegment(sketch, "E453", {"start": v(-160.37, -139.5) * mm, "end": v(-164.83, -139.5) * mm});
            skArc(sketch, "E454", {"start": v(-160.37, -139.5) * mm, "mid": v(-160.12, -139.44) * mm, "end": v(-159.93, -139.25) * mm});
            skArc(sketch, "E455", {"start": v(-159.25, -139.94) * mm, "mid": v(-159.15, -139.15) * mm, "end": v(-159.93, -139.25) * mm});
            skArc(sketch, "E456", {"start": v(-159.25, -139.94) * mm, "mid": v(-159.43, -140.12) * mm, "end": v(-159.5, -140.37) * mm});
            skLineSegment(sketch, "E457", {"start": v(-159.5, -141.94) * mm, "end": v(-159.5, -140.37) * mm});
            skArc(sketch, "E458", {"start": v(-159.5, -141.94) * mm, "mid": v(-159.43, -142.19) * mm, "end": v(-159.25, -142.37) * mm});
            skArc(sketch, "E459", {"start": v(-159.93, -143.05) * mm, "mid": v(-159.15, -143.16) * mm, "end": v(-159.25, -142.37) * mm});
            skArc(sketch, "E460", {"start": v(-159.93, -143.05) * mm, "mid": v(-160.12, -142.87) * mm, "end": v(-160.37, -142.8) * mm});
            skLineSegment(sketch, "E461", {"start": v(-164.83, -142.8) * mm, "end": v(-160.37, -142.8) * mm});
            skCircle(sketch, "E462", {"center": v(-57, 29.35) * mm, "radius": 1.55 * mm});
            skCircle(sketch, "E463", {"center": v(-57, -94.65) * mm, "radius": 1.55 * mm});
            skCircle(sketch, "E464", {"center": v(-57, 84.35) * mm, "radius": 1.55 * mm});
            skCircle(sketch, "E465", {"center": v(-67, -56.65) * mm, "radius": 1.6 * mm});
            skCircle(sketch, "E466", {"center": v(-67, 84.35) * mm, "radius": 1.55 * mm});
            skCircle(sketch, "E467", {"center": v(-67, 141.35) * mm, "radius": 1.55 * mm});
            skLineSegment(sketch, "E468", {"start": v(-130.87, -56.1) * mm, "end": v(-130.87, -49.74) * mm});
            skArc(sketch, "E469", {"start": v(-134.07, -56.1) * mm, "mid": v(-132.47, -57.7) * mm, "end": v(-130.87, -56.1) * mm});
            skLineSegment(sketch, "E470", {"start": v(-134.07, -49.74) * mm, "end": v(-134.07, -56.1) * mm});
            skArc(sketch, "E471", {"start": v(-130.87, -49.74) * mm, "mid": v(-132.47, -48.14) * mm, "end": v(-134.07, -49.74) * mm});
            skLineSegment(sketch, "E472", {"start": v(-82.6, 25.19) * mm, "end": v(-82.6, 31.54) * mm});
            skArc(sketch, "E473", {"start": v(-85.8, 25.19) * mm, "mid": v(-84.2, 23.59) * mm, "end": v(-82.6, 25.19) * mm});
            skLineSegment(sketch, "E474", {"start": v(-85.8, 31.54) * mm, "end": v(-85.8, 25.19) * mm});
            skArc(sketch, "E475", {"start": v(-82.6, 31.54) * mm, "mid": v(-84.2, 33.14) * mm, "end": v(-85.8, 31.54) * mm});
            skLineSegment(sketch, "E476", {"start": v(-82.6, -51.01) * mm, "end": v(-82.6, -49.74) * mm});
            skArc(sketch, "E477", {"start": v(-85.8, -51.01) * mm, "mid": v(-84.2, -52.61) * mm, "end": v(-82.6, -51.01) * mm});
            skLineSegment(sketch, "E478", {"start": v(-85.8, -49.74) * mm, "end": v(-85.8, -51.01) * mm});
            skArc(sketch, "E479", {"start": v(-82.6, -49.74) * mm, "mid": v(-84.2, -48.14) * mm, "end": v(-85.8, -49.74) * mm});
            skCircle(sketch, "E480", {"center": v(-89.29, 1.06) * mm, "radius": 1.6 * mm});
            skCircle(sketch, "E481", {"center": v(-138.14, 6.43) * mm, "radius": 1.6 * mm});
            skCircle(sketch, "E482", {"center": v(-68.2, -87.77) * mm, "radius": 2.1 * mm});
            skLineSegment(sketch, "E483", {"start": v(-146.5, 48.03) * mm, "end": v(-146.5, 46.03) * mm});
            skArc(sketch, "E484", {"start": v(-142.3, 48.03) * mm, "mid": v(-144.4, 50.13) * mm, "end": v(-146.5, 48.03) * mm});
            skLineSegment(sketch, "E485", {"start": v(-142.3, 46.03) * mm, "end": v(-142.3, 48.03) * mm});
            skArc(sketch, "E486", {"start": v(-146.5, 46.03) * mm, "mid": v(-144.4, 43.93) * mm, "end": v(-142.3, 46.03) * mm});
            skLineSegment(sketch, "E487", {"start": v(-70.3, 48.03) * mm, "end": v(-70.3, 46.03) * mm});
            skArc(sketch, "E488", {"start": v(-66.1, 48.03) * mm, "mid": v(-68.2, 50.13) * mm, "end": v(-70.3, 48.03) * mm});
            skLineSegment(sketch, "E489", {"start": v(-66.1, 46.03) * mm, "end": v(-66.1, 48.03) * mm});
            skArc(sketch, "E490", {"start": v(-70.3, 46.03) * mm, "mid": v(-68.2, 43.93) * mm, "end": v(-66.1, 46.03) * mm});
            skCircle(sketch, "E491", {"center": v(-96.63, -48.24) * mm, "radius": 1.6 * mm});
            skCircle(sketch, "E492", {"center": v(-147.73, -81.44) * mm, "radius": 1.6 * mm});
            skCircle(sketch, "E493", {"center": v(-117.23, 1.06) * mm, "radius": 1.6 * mm});
            skCircle(sketch, "E494", {"center": v(-89.03, -81.44) * mm, "radius": 1.6 * mm});
            skCircle(sketch, "E495", {"center": v(-158.5, -102.65) * mm, "radius": 1.6 * mm});
            skCircle(sketch, "E496", {"center": v(-158.5, 40.35) * mm, "radius": 1.6 * mm});
            skCircle(sketch, "E497", {"center": v(-144.4, -87.77) * mm, "radius": 2.1 * mm});
            skLineSegment(sketch, "E498", {"start": v(-138.14, -93.57) * mm, "end": v(-140.88, -93.57) * mm});
            skArc(sketch, "E499", {"start": v(-138.14, -96.77) * mm, "mid": v(-136.54, -95.17) * mm, "end": v(-138.14, -93.57) * mm});
            skLineSegment(sketch, "E500", {"start": v(-140.88, -96.77) * mm, "end": v(-138.14, -96.77) * mm});
            skArc(sketch, "E501", {"start": v(-140.88, -93.57) * mm, "mid": v(-142.48, -95.17) * mm, "end": v(-140.88, -96.77) * mm});
            skCircle(sketch, "E502", {"center": v(-104.88, -95.17) * mm, "radius": 1.6 * mm});
            skCircle(sketch, "E503", {"center": v(-162, -18.65) * mm, "radius": 1.55 * mm});
            skCircle(sketch, "E504", {"center": v(-162, -94.65) * mm, "radius": 1.6 * mm});
            skCircle(sketch, "E505", {"center": v(-147, -121.15) * mm, "radius": 1.6 * mm});
            skCircle(sketch, "E506", {"center": v(-107, -121.15) * mm, "radius": 1.6 * mm});
            skCircle(sketch, "E507", {"center": v(-67, -121.15) * mm, "radius": 1.6 * mm});
            skCircle(sketch, "E508", {"center": v(-135.4, -71.15) * mm, "radius": 2.23 * mm});
            skCircle(sketch, "E509", {"center": v(-132.08, -5.05) * mm, "radius": 2.23 * mm});
            skCircle(sketch, "E510", {"center": v(-151.88, 52.83) * mm, "radius": 1.6 * mm});
            skCircle(sketch, "E511", {"center": v(-73.88, -95.17) * mm, "radius": 1.6 * mm});
            skLineSegment(sketch, "E512", {"start": v(-157, 126.47) * mm, "end": v(-137, 126.47) * mm});
            skArc(sketch, "E513", {"start": v(-157, 129.22) * mm, "mid": v(-158.38, 127.85) * mm, "end": v(-157, 126.47) * mm});
            skLineSegment(sketch, "E514", {"start": v(-137, 129.22) * mm, "end": v(-157, 129.22) * mm});
            skArc(sketch, "E515", {"start": v(-137, 126.47) * mm, "mid": v(-135.63, 127.85) * mm, "end": v(-137, 129.22) * mm});
            skLineSegment(sketch, "E516", {"start": v(-157, 77.47) * mm, "end": v(-137, 77.47) * mm});
            skArc(sketch, "E517", {"start": v(-157, 80.22) * mm, "mid": v(-158.38, 78.85) * mm, "end": v(-157, 77.47) * mm});
            skLineSegment(sketch, "E518", {"start": v(-137, 80.22) * mm, "end": v(-157, 80.22) * mm});
            skArc(sketch, "E519", {"start": v(-137, 77.47) * mm, "mid": v(-135.63, 78.85) * mm, "end": v(-137, 80.22) * mm});
            skLineSegment(sketch, "E520", {"start": v(-99, 126.47) * mm, "end": v(-79, 126.47) * mm});
            skArc(sketch, "E521", {"start": v(-99, 129.22) * mm, "mid": v(-100.38, 127.85) * mm, "end": v(-99, 126.47) * mm});
            skLineSegment(sketch, "E522", {"start": v(-79, 129.22) * mm, "end": v(-99, 129.22) * mm});
            skArc(sketch, "E523", {"start": v(-79, 126.47) * mm, "mid": v(-77.63, 127.85) * mm, "end": v(-79, 129.22) * mm});
            skLineSegment(sketch, "E524", {"start": v(-99, 77.47) * mm, "end": v(-79, 77.47) * mm});
            skArc(sketch, "E525", {"start": v(-99, 80.22) * mm, "mid": v(-100.38, 78.85) * mm, "end": v(-99, 77.47) * mm});
            skLineSegment(sketch, "E526", {"start": v(-79, 80.22) * mm, "end": v(-99, 80.22) * mm});
            skArc(sketch, "E527", {"start": v(-79, 77.47) * mm, "mid": v(-77.63, 78.85) * mm, "end": v(-79, 80.22) * mm});
            skLineSegment(sketch, "E528", {"start": v(-157, 116.47) * mm, "end": v(-137, 116.47) * mm});
            skArc(sketch, "E529", {"start": v(-157, 119.22) * mm, "mid": v(-158.38, 117.85) * mm, "end": v(-157, 116.47) * mm});
            skLineSegment(sketch, "E530", {"start": v(-137, 119.22) * mm, "end": v(-157, 119.22) * mm});
            skArc(sketch, "E531", {"start": v(-137, 116.47) * mm, "mid": v(-135.63, 117.85) * mm, "end": v(-137, 119.22) * mm});
            skLineSegment(sketch, "E532", {"start": v(-157, 67.47) * mm, "end": v(-137, 67.47) * mm});
            skArc(sketch, "E533", {"start": v(-157, 70.22) * mm, "mid": v(-158.38, 68.85) * mm, "end": v(-157, 67.47) * mm});
            skLineSegment(sketch, "E534", {"start": v(-137, 70.22) * mm, "end": v(-157, 70.22) * mm});
            skArc(sketch, "E535", {"start": v(-137, 67.47) * mm, "mid": v(-135.63, 68.85) * mm, "end": v(-137, 70.22) * mm});
            skLineSegment(sketch, "E536", {"start": v(-99, 116.47) * mm, "end": v(-79, 116.47) * mm});
            skArc(sketch, "E537", {"start": v(-99, 119.22) * mm, "mid": v(-100.38, 117.85) * mm, "end": v(-99, 116.47) * mm});
            skLineSegment(sketch, "E538", {"start": v(-79, 119.22) * mm, "end": v(-99, 119.22) * mm});
            skArc(sketch, "E539", {"start": v(-79, 116.47) * mm, "mid": v(-77.63, 117.85) * mm, "end": v(-79, 119.22) * mm});
            skLineSegment(sketch, "E540", {"start": v(-99, 67.47) * mm, "end": v(-79, 67.47) * mm});
            skArc(sketch, "E541", {"start": v(-99, 70.22) * mm, "mid": v(-100.38, 68.85) * mm, "end": v(-99, 67.47) * mm});
            skLineSegment(sketch, "E542", {"start": v(-79, 70.22) * mm, "end": v(-99, 70.22) * mm});
            skArc(sketch, "E543", {"start": v(-79, 67.47) * mm, "mid": v(-77.63, 68.85) * mm, "end": v(-79, 70.22) * mm});
            skCircle(sketch, "E544", {"center": v(-77, 141.35) * mm, "radius": 1.55 * mm});
            skCircle(sketch, "E545", {"center": v(117, -156.15) * mm, "radius": 1.6 * mm});
            skCircle(sketch, "E546", {"center": v(29.25, -165.45) * mm, "radius": 1.55 * mm});
            skCircle(sketch, "E547", {"center": v(103.25, -165.45) * mm, "radius": 1.55 * mm});
            skCircle(sketch, "E548", {"center": v(29.25, -146.86) * mm, "radius": 1.55 * mm});
            skCircle(sketch, "E549", {"center": v(163.25, -146.86) * mm, "radius": 1.55 * mm});
            skSolve(sketch);
        }
        {
            var Q0;
            Q0=qSketchRegion(id+"F0",true);
            extrude(context, id + "F1", {"entities" : qUnion([Q0]), "depth" : 3 * mm, "offsetDistance" : 25 * mm});
        }
    });
